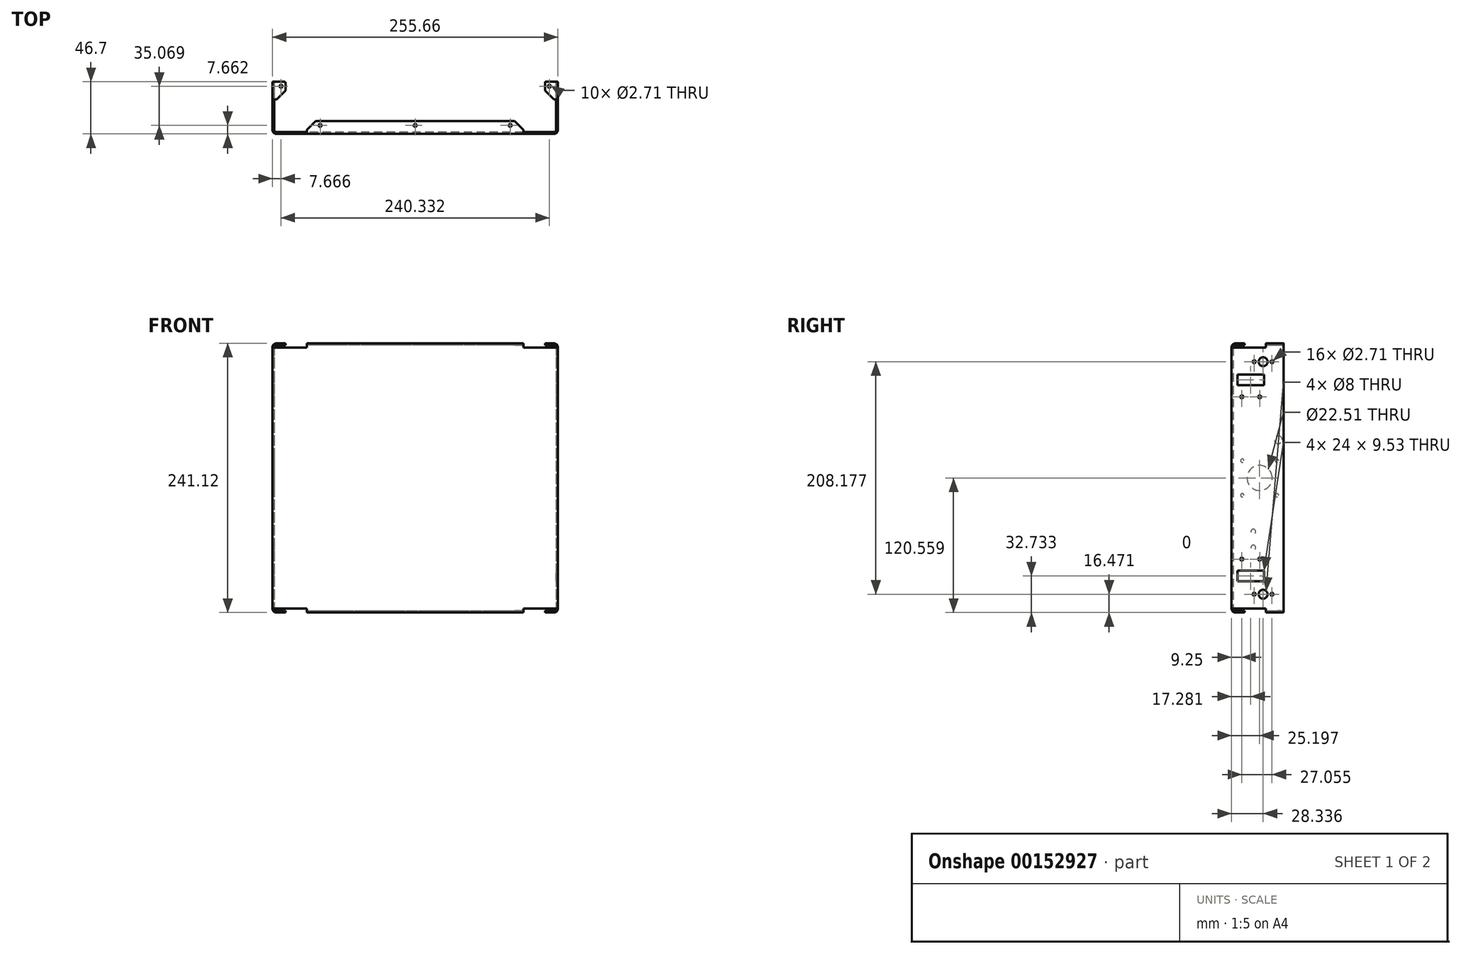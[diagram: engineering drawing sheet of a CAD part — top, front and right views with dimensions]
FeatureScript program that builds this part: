
annotation { "Feature Type Name" : "Feature", "Feature Type Description" : "" }
export const myFeature = defineFeature(function(context is Context, id is Id, definition is map)
    precondition{}
    {
        {
            var Q0;
            Q0=qCreatedBy(makeId("Top.planeOp"),FACE);
            var sketch = newSketch(context, id + "F0", { "sketchPlane" : qUnion([Q0])});
            skLineSegment(sketch, "E0.bottom", {"start": v(0, 0) * mm, "end": v(-252.24, 0) * mm});
            skLineSegment(sketch, "E0.top", {"start": v(1.7, -1.7) * mm, "end": v(-253.95, -1.7) * mm});
            skLineSegment(sketch, "E1.top", {"start": v(-252.24, 44.99) * mm, "end": v(-253.95, 44.99) * mm});
            skLineSegment(sketch, "E1.left", {"start": v(-252.24, 0) * mm, "end": v(-252.24, 44.99) * mm});
            skLineSegment(sketch, "E1.right", {"start": v(-253.95, -1.7) * mm, "end": v(-253.95, 44.99) * mm});
            skLineSegment(sketch, "E2.top", {"start": v(0, 44.99) * mm, "end": v(1.7, 44.99) * mm});
            skLineSegment(sketch, "E2.left", {"start": v(0, 0) * mm, "end": v(0, 44.99) * mm});
            skLineSegment(sketch, "E2.right", {"start": v(1.7, -1.7) * mm, "end": v(1.7, 44.99) * mm});
            skLineSegment(sketch, "E3", {"start": v(-126.12, 0) * mm, "end": v(-126.12, -1.7) * mm, "construction": true});
            skSolve(sketch);
        }
        {
            var Q0;
            Q0=qSketchRegion(id+"F0",true);
            extrude(context, id + "F1", {"entities" : qUnion([Q0]), "depth" : 233.74 * mm});
        }
        {
            var Q0;
            Q0=makeQuery(id+"F1.opExtrude","CAP_FACE",FACE,{"disambiguationData":[OSD([sQuery(id+"F0.wireOp",EDGE,"E0.bottom"),sQuery(id+"F0.wireOp",EDGE,"E0.top"),sQuery(id+"F0.wireOp",EDGE,"E1.top"),sQuery(id+"F0.wireOp",EDGE,"E1.left"),sQuery(id+"F0.wireOp",EDGE,"E1.right"),sQuery(id+"F0.wireOp",EDGE,"E2.top"),sQuery(id+"F0.wireOp",EDGE,"E2.left"),sQuery(id+"F0.wireOp",EDGE,"E2.right")])],"isStart":true});
            var sketch = newSketch(context, id + "F2", { "sketchPlane" : qUnion([Q0])});
            skLineSegment(sketch, "E4.bottom", {"start": v(1.7, -44.99) * mm, "end": v(0, -44.99) * mm});
            skLineSegment(sketch, "E4.top", {"start": v(1.7, -29.11) * mm, "end": v(0, -29.11) * mm});
            skLineSegment(sketch, "E4.left", {"start": v(1.7, -44.99) * mm, "end": v(1.7, -29.11) * mm});
            skLineSegment(sketch, "E4.right", {"start": v(0, -44.99) * mm, "end": v(0, -29.11) * mm});
            skLineSegment(sketch, "E5.bottom", {"start": v(-29.11, 0) * mm, "end": v(-223.12, 0) * mm});
            skLineSegment(sketch, "E5.top", {"start": v(-29.11, 1.7) * mm, "end": v(-223.12, 1.7) * mm});
            skLineSegment(sketch, "E5.left", {"start": v(-29.11, 0) * mm, "end": v(-29.11, 1.7) * mm});
            skLineSegment(sketch, "E5.right", {"start": v(-223.12, 0) * mm, "end": v(-223.12, 1.7) * mm});
            skLineSegment(sketch, "E6.bottom", {"start": v(-252.24, -44.99) * mm, "end": v(-253.95, -44.99) * mm});
            skLineSegment(sketch, "E6.top", {"start": v(-252.24, -29.11) * mm, "end": v(-253.95, -29.11) * mm});
            skLineSegment(sketch, "E6.left", {"start": v(-252.24, -44.99) * mm, "end": v(-252.24, -29.11) * mm});
            skLineSegment(sketch, "E6.right", {"start": v(-253.95, -44.99) * mm, "end": v(-253.95, -29.11) * mm});
            skPoint(sketch, "E7", {"position": v(-126.12, 0) * mm});
            skLineSegment(sketch, "E8", {"start": v(0, -29.11) * mm, "end": v(-29.11, -29.11) * mm, "construction": true});
            skLineSegment(sketch, "E9", {"start": v(-29.11, -29.11) * mm, "end": v(-29.11, 0) * mm, "construction": true});
            skSolve(sketch);
        }
        {
            var Q0;
            Q0=qSketchRegion(id+"F2",true);
            extrude(context, id + "F3", {"entities" : qUnion([Q0]), "operationType" : NewBodyOperationType.ADD, "depth" : 3.7 * mm});
        }
        {
            var Q0;
            Q0=makeQuery(id+"F1.opExtrude","CAP_FACE",FACE,{"disambiguationData":[OSD([sQuery(id+"F0.wireOp",EDGE,"E0.bottom"),sQuery(id+"F0.wireOp",EDGE,"E0.top"),sQuery(id+"F0.wireOp",EDGE,"E1.top"),sQuery(id+"F0.wireOp",EDGE,"E1.left"),sQuery(id+"F0.wireOp",EDGE,"E1.right"),sQuery(id+"F0.wireOp",EDGE,"E2.top"),sQuery(id+"F0.wireOp",EDGE,"E2.left"),sQuery(id+"F0.wireOp",EDGE,"E2.right")])],"isStart":false});
            var sketch = newSketch(context, id + "F4", { "sketchPlane" : qUnion([Q0])});
            skLineSegment(sketch, "E10.bottom", {"start": v(-253.95, 44.99) * mm, "end": v(-252.24, 44.99) * mm});
            skLineSegment(sketch, "E10.top", {"start": v(-253.95, 29.11) * mm, "end": v(-252.24, 29.11) * mm});
            skLineSegment(sketch, "E10.left", {"start": v(-253.95, 44.99) * mm, "end": v(-253.95, 29.11) * mm});
            skLineSegment(sketch, "E10.right", {"start": v(-252.24, 44.99) * mm, "end": v(-252.24, 29.11) * mm});
            skLineSegment(sketch, "E11.bottom", {"start": v(0, 44.99) * mm, "end": v(1.7, 44.99) * mm});
            skLineSegment(sketch, "E11.top", {"start": v(0, 29.11) * mm, "end": v(1.7, 29.11) * mm});
            skLineSegment(sketch, "E11.left", {"start": v(0, 44.99) * mm, "end": v(0, 29.11) * mm});
            skLineSegment(sketch, "E11.right", {"start": v(1.7, 44.99) * mm, "end": v(1.7, 29.11) * mm});
            skLineSegment(sketch, "E12.bottom", {"start": v(-29.11, -1.7) * mm, "end": v(-223.12, -1.7) * mm});
            skLineSegment(sketch, "E12.top", {"start": v(-29.11, 0) * mm, "end": v(-223.12, 0) * mm});
            skLineSegment(sketch, "E12.left", {"start": v(-29.11, -1.7) * mm, "end": v(-29.11, 0) * mm});
            skLineSegment(sketch, "E12.right", {"start": v(-223.12, -1.7) * mm, "end": v(-223.12, 0) * mm});
            skSolve(sketch);
        }
        {
            var Q0;
            Q0=qSketchRegion(id+"F4",true);
            extrude(context, id + "F5", {"entities" : qUnion([Q0]), "operationType" : NewBodyOperationType.ADD, "depth" : 3.7 * mm});
        }
        {
            var Q0;
            Q0=makeQuery(id+"F5.boolean.opBoolean","MERGE",FACE,{"derivedFrom":[makeQuery(id+"F3.boolean.opBoolean","MERGE",FACE,{"derivedFrom":[makeQuery(id+"F1.opExtrude","SWEPT_FACE",FACE,{"disambiguationData":[OSD([sQuery(id+"F0.wireOp",EDGE,"E0.bottom")])]}),makeQuery(id+"F3.opExtrude","SWEPT_FACE",FACE,{"disambiguationData":[OSD([sQuery(id+"F2.wireOp",EDGE,"E5.bottom")])]})]}),makeQuery(id+"F5.opExtrude","SWEPT_FACE",FACE,{"disambiguationData":[OSD([sQuery(id+"F4.wireOp",EDGE,"E12.top")])]})]});
            var sketch = newSketch(context, id + "F6", { "sketchPlane" : qUnion([Q0])});
            skLineSegment(sketch, "E13.bottom", {"start": v(223.12, -3.7) * mm, "end": v(29.11, -3.7) * mm});
            skLineSegment(sketch, "E13.top", {"start": v(223.12, -1.98) * mm, "end": v(29.11, -1.98) * mm});
            skLineSegment(sketch, "E13.left", {"start": v(223.12, -3.7) * mm, "end": v(223.12, -1.98) * mm});
            skLineSegment(sketch, "E13.right", {"start": v(29.11, -3.7) * mm, "end": v(29.11, -1.98) * mm});
            skLineSegment(sketch, "E14.bottom", {"start": v(29.11, 237.43) * mm, "end": v(223.12, 237.43) * mm});
            skLineSegment(sketch, "E14.top", {"start": v(29.11, 235.72) * mm, "end": v(223.12, 235.72) * mm});
            skLineSegment(sketch, "E14.left", {"start": v(29.11, 237.43) * mm, "end": v(29.11, 235.72) * mm});
            skLineSegment(sketch, "E14.right", {"start": v(223.12, 237.43) * mm, "end": v(223.12, 235.72) * mm});
            skSolve(sketch);
        }
        {
            var Q0;
            Q0=qSketchRegion(id+"F6",true);
            extrude(context, id + "F7", {"entities" : qUnion([Q0]), "operationType" : NewBodyOperationType.ADD, "depth" : 9.92 * mm});
        }
        {
            var Q0;
            Q0=makeQuery(id+"F5.boolean.opBoolean","MERGE",FACE,{"derivedFrom":[makeQuery(id+"F3.boolean.opBoolean","MERGE",FACE,{"derivedFrom":[makeQuery(id+"F1.opExtrude","SWEPT_FACE",FACE,{"disambiguationData":[OSD([sQuery(id+"F0.wireOp",EDGE,"E1.left")])]}),makeQuery(id+"F3.opExtrude","SWEPT_FACE",FACE,{"disambiguationData":[OSD([sQuery(id+"F2.wireOp",EDGE,"E6.left")])]})]}),makeQuery(id+"F5.opExtrude","SWEPT_FACE",FACE,{"disambiguationData":[OSD([sQuery(id+"F4.wireOp",EDGE,"E10.right")])]})]});
            var sketch = newSketch(context, id + "F8", { "sketchPlane" : qUnion([Q0])});
            skLineSegment(sketch, "E15.bottom", {"start": v(29.11, 237.43) * mm, "end": v(44.99, 237.43) * mm});
            skLineSegment(sketch, "E15.top", {"start": v(29.11, 235.72) * mm, "end": v(44.99, 235.72) * mm});
            skLineSegment(sketch, "E15.left", {"start": v(29.11, 237.43) * mm, "end": v(29.11, 235.72) * mm});
            skLineSegment(sketch, "E15.right", {"start": v(44.99, 237.43) * mm, "end": v(44.99, 235.72) * mm});
            skLineSegment(sketch, "E16.bottom", {"start": v(29.11, -3.7) * mm, "end": v(44.99, -3.7) * mm});
            skLineSegment(sketch, "E16.top", {"start": v(29.11, -1.98) * mm, "end": v(44.99, -1.98) * mm});
            skLineSegment(sketch, "E16.left", {"start": v(29.11, -3.7) * mm, "end": v(29.11, -1.98) * mm});
            skLineSegment(sketch, "E16.right", {"start": v(44.99, -3.7) * mm, "end": v(44.99, -1.98) * mm});
            skSolve(sketch);
        }
        {
            var Q0;
            Q0=qSketchRegion(id+"F8",true);
            extrude(context, id + "F9", {"entities" : qUnion([Q0]), "operationType" : NewBodyOperationType.ADD, "depth" : 9.92 * mm});
        }
        {
            var Q0;
            Q0=makeQuery(id+"F5.boolean.opBoolean","MERGE",FACE,{"derivedFrom":[makeQuery(id+"F3.boolean.opBoolean","MERGE",FACE,{"derivedFrom":[makeQuery(id+"F1.opExtrude","SWEPT_FACE",FACE,{"disambiguationData":[OSD([sQuery(id+"F0.wireOp",EDGE,"E2.left")])]}),makeQuery(id+"F3.opExtrude","SWEPT_FACE",FACE,{"disambiguationData":[OSD([sQuery(id+"F2.wireOp",EDGE,"E4.right")])]})]}),makeQuery(id+"F5.opExtrude","SWEPT_FACE",FACE,{"disambiguationData":[OSD([sQuery(id+"F4.wireOp",EDGE,"E11.left")])]})]});
            var sketch = newSketch(context, id + "F10", { "sketchPlane" : qUnion([Q0])});
            skLineSegment(sketch, "E17.bottom", {"start": v(-29.11, -3.7) * mm, "end": v(-44.99, -3.7) * mm});
            skLineSegment(sketch, "E17.top", {"start": v(-29.11, -1.98) * mm, "end": v(-44.99, -1.98) * mm});
            skLineSegment(sketch, "E17.left", {"start": v(-29.11, -3.7) * mm, "end": v(-29.11, -1.98) * mm});
            skLineSegment(sketch, "E17.right", {"start": v(-44.99, -3.7) * mm, "end": v(-44.99, -1.98) * mm});
            skLineSegment(sketch, "E18.bottom", {"start": v(-29.11, 237.43) * mm, "end": v(-44.99, 237.43) * mm});
            skLineSegment(sketch, "E18.top", {"start": v(-29.11, 235.72) * mm, "end": v(-44.99, 235.72) * mm});
            skLineSegment(sketch, "E18.left", {"start": v(-29.11, 237.43) * mm, "end": v(-29.11, 235.72) * mm});
            skLineSegment(sketch, "E18.right", {"start": v(-44.99, 237.43) * mm, "end": v(-44.99, 235.72) * mm});
            skSolve(sketch);
        }
        {
            var Q0;
            Q0=qSketchRegion(id+"F10",true);
            extrude(context, id + "F11", {"entities" : qUnion([Q0]), "operationType" : NewBodyOperationType.ADD, "depth" : 9.92 * mm});
        }
        {
            var Q0;
            Q0=makeQuery(id+"F11.opExtrude","CAP_EDGE",EDGE,{"disambiguationData":[OSD([sQuery(id+"F10.wireOp",EDGE,"E18.top")])],"isStart":true});
            var Q1;
            Q1=makeQuery(id+"F7.opExtrude","CAP_EDGE",EDGE,{"disambiguationData":[OSD([sQuery(id+"F6.wireOp",EDGE,"E14.top")])],"isStart":true});
            var Q2;
            Q2=makeQuery(id+"F9.opExtrude","CAP_EDGE",EDGE,{"disambiguationData":[OSD([sQuery(id+"F8.wireOp",EDGE,"E15.top")])],"isStart":true});
            var Q3;
            Q3=makeQuery(id+"F9.opExtrude","CAP_EDGE",EDGE,{"disambiguationData":[OSD([sQuery(id+"F8.wireOp",EDGE,"E16.top")])],"isStart":true});
            var Q4;
            Q4=makeQuery(id+"F7.opExtrude","CAP_EDGE",EDGE,{"disambiguationData":[OSD([sQuery(id+"F6.wireOp",EDGE,"E13.top")])],"isStart":true});
            var Q5;
            Q5=makeQuery(id+"F11.opExtrude","CAP_EDGE",EDGE,{"disambiguationData":[OSD([sQuery(id+"F10.wireOp",EDGE,"E17.top")])],"isStart":true});
            var Q6;
            Q6=makeQuery(id+"F1.opExtrude","SWEPT_EDGE",EDGE,{"disambiguationData":[OSD([sQuery(id+"F0.wireOp",EDGE,"E0.bottom"),sQuery(id+"F0.wireOp",EDGE,"E2.left")])]});
            var Q7;
            Q7=makeQuery(id+"F1.opExtrude","SWEPT_EDGE",EDGE,{"disambiguationData":[OSD([sQuery(id+"F0.wireOp",EDGE,"E0.bottom"),sQuery(id+"F0.wireOp",EDGE,"E1.left")])]});
            fillet(context, id + "F12", {"entities" : qUnion([Q0, Q1, Q2, Q3, Q4, Q5, Q6, Q7]), "radius" : 1.98 * mm, "tangentPropagation" : true, "allowEdgeOverflow" : false});
        }
        {
            var Q0;
            Q0=makeQuery(id+"F3.opExtrude","CAP_EDGE",EDGE,{"disambiguationData":[OSD([sQuery(id+"F2.wireOp",EDGE,"E6.right")])],"isStart":false});
            var Q1;
            Q1=makeQuery(id+"F3.opExtrude","CAP_EDGE",EDGE,{"disambiguationData":[OSD([sQuery(id+"F2.wireOp",EDGE,"E5.top")])],"isStart":false});
            var Q2;
            Q2=makeQuery(id+"F1.opExtrude","SWEPT_EDGE",EDGE,{"disambiguationData":[OSD([sQuery(id+"F0.wireOp",EDGE,"E0.top"),sQuery(id+"F0.wireOp",EDGE,"E1.right")])]});
            var Q3;
            Q3=makeQuery(id+"F5.opExtrude","CAP_EDGE",EDGE,{"disambiguationData":[OSD([sQuery(id+"F4.wireOp",EDGE,"E12.bottom")])],"isStart":false});
            var Q4;
            Q4=makeQuery(id+"F5.opExtrude","CAP_EDGE",EDGE,{"disambiguationData":[OSD([sQuery(id+"F4.wireOp",EDGE,"E10.left")])],"isStart":false});
            var Q5;
            Q5=makeQuery(id+"F3.opExtrude","CAP_EDGE",EDGE,{"disambiguationData":[OSD([sQuery(id+"F2.wireOp",EDGE,"E4.left")])],"isStart":false});
            var Q6;
            Q6=makeQuery(id+"F1.opExtrude","SWEPT_EDGE",EDGE,{"disambiguationData":[OSD([sQuery(id+"F0.wireOp",EDGE,"E0.top"),sQuery(id+"F0.wireOp",EDGE,"E2.right")])]});
            var Q7;
            Q7=makeQuery(id+"F5.opExtrude","CAP_EDGE",EDGE,{"disambiguationData":[OSD([sQuery(id+"F4.wireOp",EDGE,"E11.right")])],"isStart":false});
            fillet(context, id + "F13", {"entities" : qUnion([Q0, Q1, Q2, Q3, Q4, Q5, Q6, Q7]), "radius" : 3.7 * mm, "tangentPropagation" : true, "allowEdgeOverflow" : false});
        }
        {
            var Q0;
            Q0=makeQuery(id+"F9.opExtrude","CAP_EDGE",EDGE,{"disambiguationData":[OSD([sQuery(id+"F8.wireOp",EDGE,"E15.left")])],"isStart":false});
            var Q1;
            Q1=makeQuery(id+"F7.opExtrude","CAP_EDGE",EDGE,{"disambiguationData":[OSD([sQuery(id+"F6.wireOp",EDGE,"E14.right")])],"isStart":false});
            var Q2;
            Q2=makeQuery(id+"F7.opExtrude","CAP_EDGE",EDGE,{"disambiguationData":[OSD([sQuery(id+"F6.wireOp",EDGE,"E14.left")])],"isStart":false});
            var Q3;
            Q3=makeQuery(id+"F11.opExtrude","CAP_EDGE",EDGE,{"disambiguationData":[OSD([sQuery(id+"F10.wireOp",EDGE,"E18.left")])],"isStart":false});
            var Q4;
            Q4=makeQuery(id+"F7.opExtrude","CAP_EDGE",EDGE,{"disambiguationData":[OSD([sQuery(id+"F6.wireOp",EDGE,"E13.right")])],"isStart":false});
            var Q5;
            Q5=makeQuery(id+"F11.opExtrude","CAP_EDGE",EDGE,{"disambiguationData":[OSD([sQuery(id+"F10.wireOp",EDGE,"E17.left")])],"isStart":false});
            var Q6;
            Q6=makeQuery(id+"F9.opExtrude","CAP_EDGE",EDGE,{"disambiguationData":[OSD([sQuery(id+"F8.wireOp",EDGE,"E16.left")])],"isStart":false});
            var Q7;
            Q7=makeQuery(id+"F7.opExtrude","CAP_EDGE",EDGE,{"disambiguationData":[OSD([sQuery(id+"F6.wireOp",EDGE,"E13.left")])],"isStart":false});
            chamfer(context, id + "F14", {"entities" : qUnion([Q0, Q1, Q2, Q3, Q4, Q5, Q6, Q7]), "width" : 7.94 * mm, "tangentPropagation" : true});
        }
        {
            var Q0;
            Q0=makeQuery(id+"F7.boolean.opBoolean","MERGE",FACE,{"derivedFrom":[makeQuery(id+"F3.opExtrude","CAP_FACE",FACE,{"disambiguationData":[OSD([sQuery(id+"F2.wireOp",EDGE,"E5.bottom"),sQuery(id+"F2.wireOp",EDGE,"E5.top"),sQuery(id+"F2.wireOp",EDGE,"E5.left"),sQuery(id+"F2.wireOp",EDGE,"E5.right")])],"isStart":false}),makeQuery(id+"F7.opExtrude","SWEPT_FACE",FACE,{"disambiguationData":[OSD([sQuery(id+"F6.wireOp",EDGE,"E13.bottom")])]})]});
            var sketch = newSketch(context, id + "F15", { "sketchPlane" : qUnion([Q0])});
            skLineSegment(sketch, "E19", {"start": v(-33.08, -5.95) * mm, "end": v(-41.02, -5.95) * mm, "construction": true});
            skLineSegment(sketch, "E20", {"start": v(-41.02, -5.95) * mm, "end": v(-126.12, -5.95) * mm, "construction": true});
            skLineSegment(sketch, "E21", {"start": v(-126.12, -5.95) * mm, "end": v(-211.22, -5.95) * mm, "construction": true});
            skLineSegment(sketch, "E22", {"start": v(-211.22, -5.95) * mm, "end": v(-219.15, -5.95) * mm, "construction": true});
            skCircle(sketch, "E23", {"center": v(-41.02, -5.95) * mm, "radius": 1.35 * mm});
            skCircle(sketch, "E24", {"center": v(-126.12, -5.95) * mm, "radius": 1.35 * mm});
            skCircle(sketch, "E25", {"center": v(-211.22, -5.95) * mm, "radius": 1.35 * mm});
            skLineSegment(sketch, "E26", {"start": v(-5.95, -33.08) * mm, "end": v(-5.95, -41.02) * mm, "construction": true});
            skLineSegment(sketch, "E27", {"start": v(-246.28, -33.08) * mm, "end": v(-246.28, -41.02) * mm, "construction": true});
            skCircle(sketch, "E28", {"center": v(-246.28, -41.02) * mm, "radius": 1.35 * mm});
            skCircle(sketch, "E29", {"center": v(-5.95, -41.02) * mm, "radius": 1.35 * mm});
            skSolve(sketch);
        }
        {
            var Q0;
            Q0=qSketchRegion(id+"F15",true);
            var Q1;
            Q1=makeQuery(id+"F7.boolean.opBoolean","MERGE",FACE,{"derivedFrom":[makeQuery(id+"F5.opExtrude","CAP_FACE",FACE,{"disambiguationData":[OSD([sQuery(id+"F4.wireOp",EDGE,"E12.bottom"),sQuery(id+"F4.wireOp",EDGE,"E12.top"),sQuery(id+"F4.wireOp",EDGE,"E12.left"),sQuery(id+"F4.wireOp",EDGE,"E12.right")])],"isStart":false}),makeQuery(id+"F7.opExtrude","SWEPT_FACE",FACE,{"disambiguationData":[OSD([sQuery(id+"F6.wireOp",EDGE,"E14.bottom")])]})]});
            extrude(context, id + "F16", {"entities" : qUnion([Q0]), "operationType" : NewBodyOperationType.REMOVE, "endBound" : BoundingType.UP_TO_SURFACE, "oppositeDirection" : true, "endBoundEntityFace" : qUnion([Q1]), "depth" : 25.4 * mm});
        }
        {
            var Q0;
            Q0=makeQuery(id+"F5.boolean.opBoolean","MERGE",FACE,{"derivedFrom":[makeQuery(id+"F3.boolean.opBoolean","MERGE",FACE,{"derivedFrom":[makeQuery(id+"F1.opExtrude","SWEPT_FACE",FACE,{"disambiguationData":[OSD([sQuery(id+"F0.wireOp",EDGE,"E1.right")])]}),makeQuery(id+"F3.opExtrude","SWEPT_FACE",FACE,{"disambiguationData":[OSD([sQuery(id+"F2.wireOp",EDGE,"E6.right")])]})]}),makeQuery(id+"F5.opExtrude","SWEPT_FACE",FACE,{"disambiguationData":[OSD([sQuery(id+"F4.wireOp",EDGE,"E10.left")])]})]});
            var sketch = newSketch(context, id + "F17", { "sketchPlane" : qUnion([Q0])});
            skLineSegment(sketch, "E30", {"start": v(-44.99, 12.78) * mm, "end": v(-34.6, 12.78) * mm, "construction": true});
            skLineSegment(sketch, "E31", {"start": v(-34.6, 12.78) * mm, "end": v(-18.66, 12.78) * mm, "construction": true});
            skLineSegment(sketch, "E32", {"start": v(-34.6, 12.78) * mm, "end": v(-34.6, 0) * mm, "construction": true});
            skLineSegment(sketch, "E33", {"start": v(-34.6, 233.74) * mm, "end": v(-34.6, 220.96) * mm, "construction": true});
            skLineSegment(sketch, "E34", {"start": v(-34.6, 220.96) * mm, "end": v(-18.66, 220.96) * mm, "construction": true});
            skCircle(sketch, "E35", {"center": v(-34.6, 12.78) * mm, "radius": 1.35 * mm});
            skCircle(sketch, "E36", {"center": v(-18.66, 12.78) * mm, "radius": 1.35 * mm});
            skCircle(sketch, "E37", {"center": v(-18.66, 220.96) * mm, "radius": 1.35 * mm});
            skCircle(sketch, "E38", {"center": v(-34.6, 220.96) * mm, "radius": 1.35 * mm});
            skCircle(sketch, "E39", {"center": v(-26.63, 220.96) * mm, "radius": 4 * mm});
            skCircle(sketch, "E40", {"center": v(-26.63, 12.78) * mm, "radius": 4 * mm});
            skCircle(sketch, "E41", {"center": v(-34.6, 12.78) * mm, "radius": 3.97 * mm, "construction": true});
            skLineSegment(sketch, "E42.bottom", {"start": v(-27.57, 209.46) * mm, "end": v(-3.57, 209.46) * mm});
            skLineSegment(sketch, "E42.top", {"start": v(-27.57, 199.93) * mm, "end": v(-3.57, 199.93) * mm});
            skLineSegment(sketch, "E42.left", {"start": v(-27.57, 209.46) * mm, "end": v(-27.57, 199.93) * mm});
            skLineSegment(sketch, "E42.right", {"start": v(-3.57, 209.46) * mm, "end": v(-3.57, 199.93) * mm});
            skLineSegment(sketch, "E43.bottom", {"start": v(-27.57, 24.28) * mm, "end": v(-3.57, 24.28) * mm});
            skLineSegment(sketch, "E43.top", {"start": v(-27.57, 33.8) * mm, "end": v(-3.57, 33.8) * mm});
            skLineSegment(sketch, "E43.left", {"start": v(-27.57, 24.28) * mm, "end": v(-27.57, 33.8) * mm});
            skLineSegment(sketch, "E43.right", {"start": v(-3.57, 24.28) * mm, "end": v(-3.57, 33.8) * mm});
            skLineSegment(sketch, "E44", {"start": v(-27.57, 29.04) * mm, "end": v(-44.99, 29.04) * mm, "construction": true});
            skLineSegment(sketch, "E45", {"start": v(-3.57, 29.04) * mm, "end": v(-1.98, 29.04) * mm, "construction": true});
            skLineSegment(sketch, "E46", {"start": v(-15.57, 24.28) * mm, "end": v(-15.57, 18.53) * mm, "construction": true});
            skLineSegment(sketch, "E47", {"start": v(-15.57, 18.53) * mm, "end": v(-26.63, 18.53) * mm, "construction": true});
            skLineSegment(sketch, "E48", {"start": v(-26.63, 12.78) * mm, "end": v(-26.63, 18.53) * mm, "construction": true});
            skLineSegment(sketch, "E49", {"start": v(-27.57, 33.8) * mm, "end": v(-27.57, 44.2) * mm, "construction": true});
            skLineSegment(sketch, "E50", {"start": v(-27.57, 44.2) * mm, "end": v(-23.6, 44.2) * mm, "construction": true});
            skLineSegment(sketch, "E51", {"start": v(-23.6, 44.2) * mm, "end": v(-7.54, 44.2) * mm, "construction": true});
            skLineSegment(sketch, "E52", {"start": v(-15.57, 44.2) * mm, "end": v(-15.57, 33.8) * mm, "construction": true});
            skCircle(sketch, "E53", {"center": v(-23.6, 44.2) * mm, "radius": 1.35 * mm});
            skCircle(sketch, "E54", {"center": v(-7.54, 44.2) * mm, "radius": 1.35 * mm});
            skLineSegment(sketch, "E55", {"start": v(-15.57, 199.93) * mm, "end": v(-15.57, 189.53) * mm, "construction": true});
            skLineSegment(sketch, "E56", {"start": v(-23.6, 189.53) * mm, "end": v(-7.54, 189.53) * mm, "construction": true});
            skLineSegment(sketch, "E57", {"start": v(-3.57, 204.7) * mm, "end": v(-1.98, 204.7) * mm, "construction": true});
            skLineSegment(sketch, "E58", {"start": v(-27.57, 204.7) * mm, "end": v(-44.99, 204.7) * mm, "construction": true});
            skCircle(sketch, "E59", {"center": v(-23.6, 189.53) * mm, "radius": 1.35 * mm});
            skCircle(sketch, "E60", {"center": v(-7.54, 189.53) * mm, "radius": 1.35 * mm});
            skLineSegment(sketch, "E61", {"start": v(-26.63, 220.96) * mm, "end": v(-26.63, 215.2) * mm, "construction": true});
            skLineSegment(sketch, "E62", {"start": v(-26.63, 215.2) * mm, "end": v(-15.57, 215.2) * mm, "construction": true});
            skLineSegment(sketch, "E63", {"start": v(-15.57, 215.2) * mm, "end": v(-15.57, 209.46) * mm, "construction": true});
            skSolve(sketch);
        }
        {
            var Q0;
            Q0=qSketchRegion(id+"F17",true);
            var Q1;
            Q1=makeQuery(id+"F5.boolean.opBoolean","MERGE",FACE,{"derivedFrom":[makeQuery(id+"F3.boolean.opBoolean","MERGE",FACE,{"derivedFrom":[makeQuery(id+"F1.opExtrude","SWEPT_FACE",FACE,{"disambiguationData":[OSD([sQuery(id+"F0.wireOp",EDGE,"E2.right")])]}),makeQuery(id+"F3.opExtrude","SWEPT_FACE",FACE,{"disambiguationData":[OSD([sQuery(id+"F2.wireOp",EDGE,"E4.left")])]})]}),makeQuery(id+"F5.opExtrude","SWEPT_FACE",FACE,{"disambiguationData":[OSD([sQuery(id+"F4.wireOp",EDGE,"E11.right")])]})]});
            extrude(context, id + "F18", {"entities" : qUnion([Q0]), "operationType" : NewBodyOperationType.REMOVE, "endBound" : BoundingType.UP_TO_SURFACE, "oppositeDirection" : true, "endBoundEntityFace" : qUnion([Q1]), "depth" : 25.4 * mm});
        }
        {
            var Q0;
            Q0=makeQuery(id+"F9.opExtrude","CAP_EDGE",EDGE,{"disambiguationData":[OSD([sQuery(id+"F8.wireOp",EDGE,"E16.right")])],"isStart":false});
            var Q1;
            Q1=makeQuery(id+"F9.opExtrude","CAP_EDGE",EDGE,{"disambiguationData":[OSD([sQuery(id+"F8.wireOp",EDGE,"E15.right")])],"isStart":false});
            var Q2;
            Q2=makeQuery(id+"F11.opExtrude","CAP_EDGE",EDGE,{"disambiguationData":[OSD([sQuery(id+"F10.wireOp",EDGE,"E18.right")])],"isStart":false});
            var Q3;
            Q3=makeQuery(id+"F11.opExtrude","CAP_EDGE",EDGE,{"disambiguationData":[OSD([sQuery(id+"F10.wireOp",EDGE,"E17.right")])],"isStart":false});
            fillet(context, id + "F19", {"entities" : qUnion([Q0, Q1, Q2, Q3]), "radius" : 0.76 * mm, "tangentPropagation" : true, "allowEdgeOverflow" : false});
        }
        {
            var Q0;
            Q0=makeQuery(id+"F5.boolean.opBoolean","MERGE",FACE,{"derivedFrom":[makeQuery(id+"F3.boolean.opBoolean","MERGE",FACE,{"derivedFrom":[makeQuery(id+"F1.opExtrude","SWEPT_FACE",FACE,{"disambiguationData":[OSD([sQuery(id+"F0.wireOp",EDGE,"E1.right")])]}),makeQuery(id+"F3.opExtrude","SWEPT_FACE",FACE,{"disambiguationData":[OSD([sQuery(id+"F2.wireOp",EDGE,"E6.right")])]})]}),makeQuery(id+"F5.opExtrude","SWEPT_FACE",FACE,{"disambiguationData":[OSD([sQuery(id+"F4.wireOp",EDGE,"E10.left")])]})]});
            var sketch = newSketch(context, id + "F20", { "sketchPlane" : qUnion([Q0])});
            skLineSegment(sketch, "E64", {"start": v(-44.99, 116.87) * mm, "end": v(-23.49, 116.87) * mm, "construction": true});
            skLineSegment(sketch, "E65.bottom", {"start": v(-38.99, 132.37) * mm, "end": v(-7.99, 132.37) * mm, "construction": true});
            skLineSegment(sketch, "E65.top", {"start": v(-38.99, 101.37) * mm, "end": v(-7.99, 101.37) * mm, "construction": true});
            skLineSegment(sketch, "E65.left", {"start": v(-38.99, 132.37) * mm, "end": v(-38.99, 101.37) * mm, "construction": true});
            skLineSegment(sketch, "E65.right", {"start": v(-7.99, 132.37) * mm, "end": v(-7.99, 101.37) * mm, "construction": true});
            skCircle(sketch, "E66", {"center": v(-23.49, 116.87) * mm, "radius": 11.25 * mm});
            skCircle(sketch, "E67", {"center": v(-38.99, 132.37) * mm, "radius": 1.5 * mm});
            skCircle(sketch, "E68", {"center": v(-7.99, 132.37) * mm, "radius": 1.5 * mm});
            skCircle(sketch, "E69", {"center": v(-7.99, 101.37) * mm, "radius": 1.5 * mm});
            skCircle(sketch, "E70", {"center": v(-38.99, 101.37) * mm, "radius": 1.5 * mm});
            skLineSegment(sketch, "E71", {"start": v(-23.49, 138.37) * mm, "end": v(-23.49, 116.87) * mm, "construction": true});
            skLineSegment(sketch, "E72", {"start": v(-40.24, 151.07) * mm, "end": v(-40.24, 138.37) * mm, "construction": true});
            skCircle(sketch, "E73", {"center": v(-40.24, 151.07) * mm, "radius": 3.5 * mm});
            skLineSegment(sketch, "E74", {"start": v(-40.24, 151.07) * mm, "end": v(-44.99, 151.07) * mm, "construction": true});
            skLineSegment(sketch, "E75", {"start": v(-23.49, 138.37) * mm, "end": v(-40.24, 138.37) * mm, "construction": true});
            skLineSegment(sketch, "E76", {"start": v(-23.49, 68.83) * mm, "end": v(-23.49, 116.87) * mm, "construction": true});
            skCircle(sketch, "E77", {"center": v(-17.84, 68.83) * mm, "radius": 2.15 * mm});
            skCircle(sketch, "E78", {"center": v(-17.84, 54.55) * mm, "radius": 2.15 * mm});
            skLineSegment(sketch, "E79", {"start": v(-17.84, 68.83) * mm, "end": v(-23.49, 68.83) * mm, "construction": true});
            skLineSegment(sketch, "E80", {"start": v(-17.84, 54.55) * mm, "end": v(-17.84, 68.83) * mm, "construction": true});
            skLineSegment(sketch, "E81", {"start": v(-17.84, 54.55) * mm, "end": v(-44.99, 54.55) * mm, "construction": true});
            skPoint(sketch, "E82", {"position": v(-17.84, 61.69) * mm});
            skPoint(sketch, "E83", {"position": v(-3.57, 29.04) * mm});
            skLineSegment(sketch, "E84", {"start": v(-7.54, 44.2) * mm, "end": v(-7.54, 54.55) * mm, "construction": true});
            skLineSegment(sketch, "E85", {"start": v(-7.54, 54.55) * mm, "end": v(-17.84, 54.55) * mm, "construction": true});
            skSolve(sketch);
        }
        {
            var Q0;
            Q0=qSketchRegion(id+"F20",true);
            var Q1;
            Q1=makeQuery(id+"F5.boolean.opBoolean","MERGE",FACE,{"derivedFrom":[makeQuery(id+"F3.boolean.opBoolean","MERGE",FACE,{"derivedFrom":[makeQuery(id+"F1.opExtrude","SWEPT_FACE",FACE,{"disambiguationData":[OSD([sQuery(id+"F0.wireOp",EDGE,"E1.left")])]}),makeQuery(id+"F3.opExtrude","SWEPT_FACE",FACE,{"disambiguationData":[OSD([sQuery(id+"F2.wireOp",EDGE,"E6.left")])]})]}),makeQuery(id+"F5.opExtrude","SWEPT_FACE",FACE,{"disambiguationData":[OSD([sQuery(id+"F4.wireOp",EDGE,"E10.right")])]})]});
            extrude(context, id + "F21", {"entities" : qUnion([Q0]), "operationType" : NewBodyOperationType.REMOVE, "endBound" : BoundingType.UP_TO_SURFACE, "oppositeDirection" : true, "endBoundEntityFace" : qUnion([Q1]), "depth" : 25.4 * mm});
        }
    });
